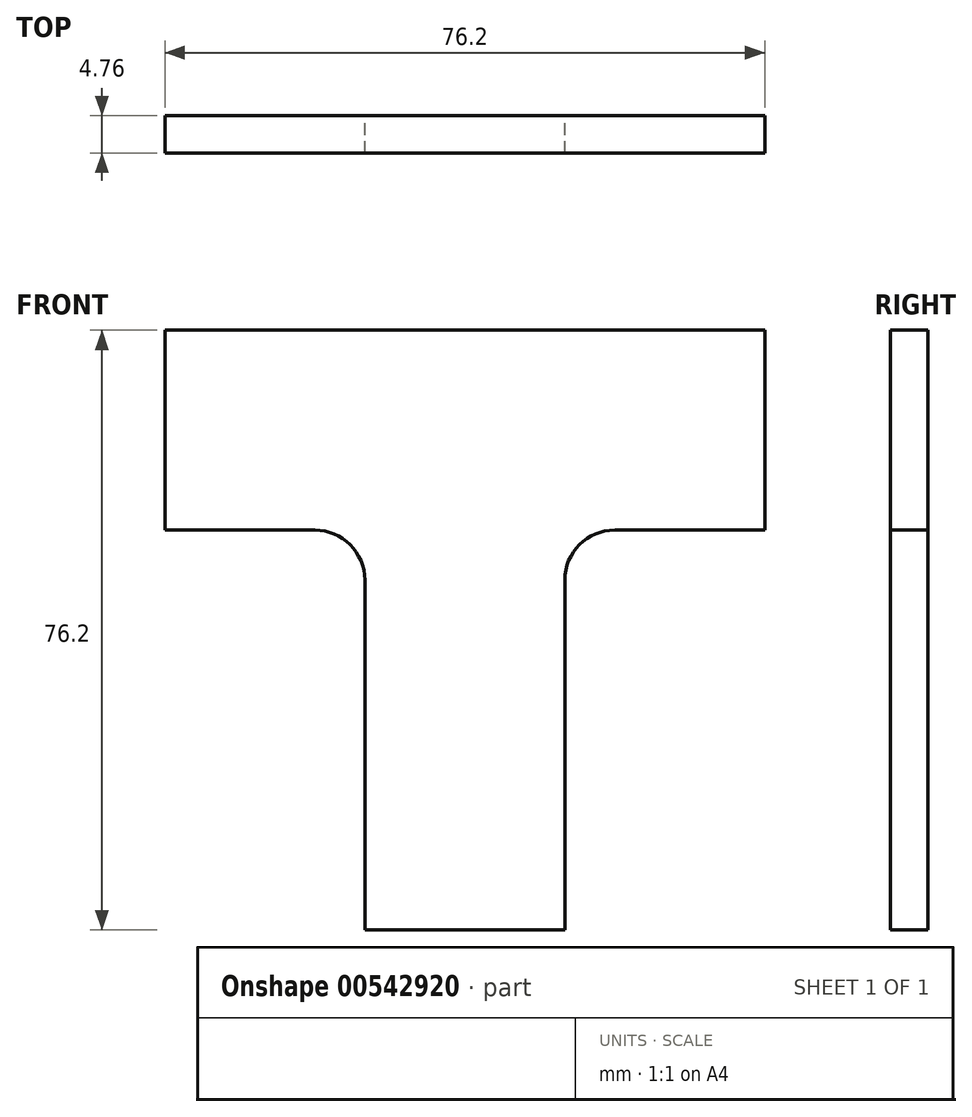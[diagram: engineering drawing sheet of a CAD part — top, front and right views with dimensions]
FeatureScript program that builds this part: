
annotation { "Feature Type Name" : "Feature", "Feature Type Description" : "" }
export const myFeature = defineFeature(function(context is Context, id is Id, definition is map)
    precondition{}
    {
        {
            var Q0;
            Q0=qCreatedBy(makeId("Front.planeOp"),FACE);
            var sketch = newSketch(context, id + "F0", { "sketchPlane" : qUnion([Q0])});
            skLineSegment(sketch, "E0", {"start": v(0, 0) * mm, "end": v(76.2, 0) * mm});
            skLineSegment(sketch, "E1", {"start": v(0, 0) * mm, "end": v(0, -25.4) * mm});
            skLineSegment(sketch, "E2", {"start": v(76.2, 0) * mm, "end": v(76.2, -25.4) * mm});
            skLineSegment(sketch, "E3", {"start": v(0, -25.4) * mm, "end": v(19.05, -25.4) * mm});
            skLineSegment(sketch, "E4", {"start": v(76.2, -25.4) * mm, "end": v(57.15, -25.4) * mm});
            skLineSegment(sketch, "E5", {"start": v(25.4, -31.75) * mm, "end": v(25.4, -76.2) * mm});
            skLineSegment(sketch, "E6", {"start": v(50.8, -31.75) * mm, "end": v(50.8, -76.2) * mm});
            skLineSegment(sketch, "E7", {"start": v(50.8, -76.2) * mm, "end": v(25.4, -76.2) * mm});
            skPoint(sketch, "E8.visualSharp", {"position": v(25.4, -25.4) * mm});
            skArc(sketch, "E8.filletArc", {"start": v(25.4, -31.75) * mm, "mid": v(23.54, -27.26) * mm, "end": v(19.05, -25.4) * mm});
            skPoint(sketch, "E9.visualSharp", {"position": v(50.8, -25.4) * mm});
            skArc(sketch, "E9.filletArc", {"start": v(57.15, -25.4) * mm, "mid": v(52.66, -27.26) * mm, "end": v(50.8, -31.75) * mm});
            skSolve(sketch);
        }
        {
            var Q0;
            Q0=makeQuery(id+"F0.imprint","IMPRINT",FACE,{"disambiguationData":[TD([[makeQuery(id+"F0.imprint","IMPRINT",EDGE,{"derivedFrom":sQuery(id+"F0.wireOp",EDGE,"E0")}),-1.0]])]});
            extrude(context, id + "F1", {"entities" : qUnion([Q0]), "depth" : 4.76 * mm, "offsetDistance" : 25.4 * mm});
        }
    });
